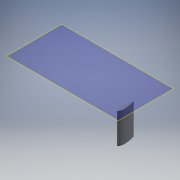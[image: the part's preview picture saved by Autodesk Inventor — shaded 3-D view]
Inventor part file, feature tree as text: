
AUTODESK INVENTOR PART (.ipt)
format: ipt  version: 2017 (Build 210142000, 142)  size: 107,008 bytes
history: native  units: mm
features: other x3, plane x1, extrude x1, fillet x1, sketch x1, reference x1
ambient origin geometry x8: Origin, YZ Plane, XZ Plane, XY Plane, X Axis, Y Axis, Z Axis, Center Point
bodies: Volumenkörper1 (feature_tree)
feature tree (8):
  plane  "Arbeitsebene1"
  extrude  "Extrusion1"  Depth=9.0mm
  fillet  "Rundung2"  [1 undecoded]
  sketch  "Skizze1"  dims[d2=600.0mm d3=0.0mm d5=9.0mm]
  reference  "Referenz1"
  other  "Baugruppe1"
  other  "Schreibtisch"
  other  "Arbeitsplatte:1"
note: 1 required parameter value undecoded (feature->parameter linkage not recoverable at this tier; creation-order binding heuristic only, values carry confidence <= 0.55)
